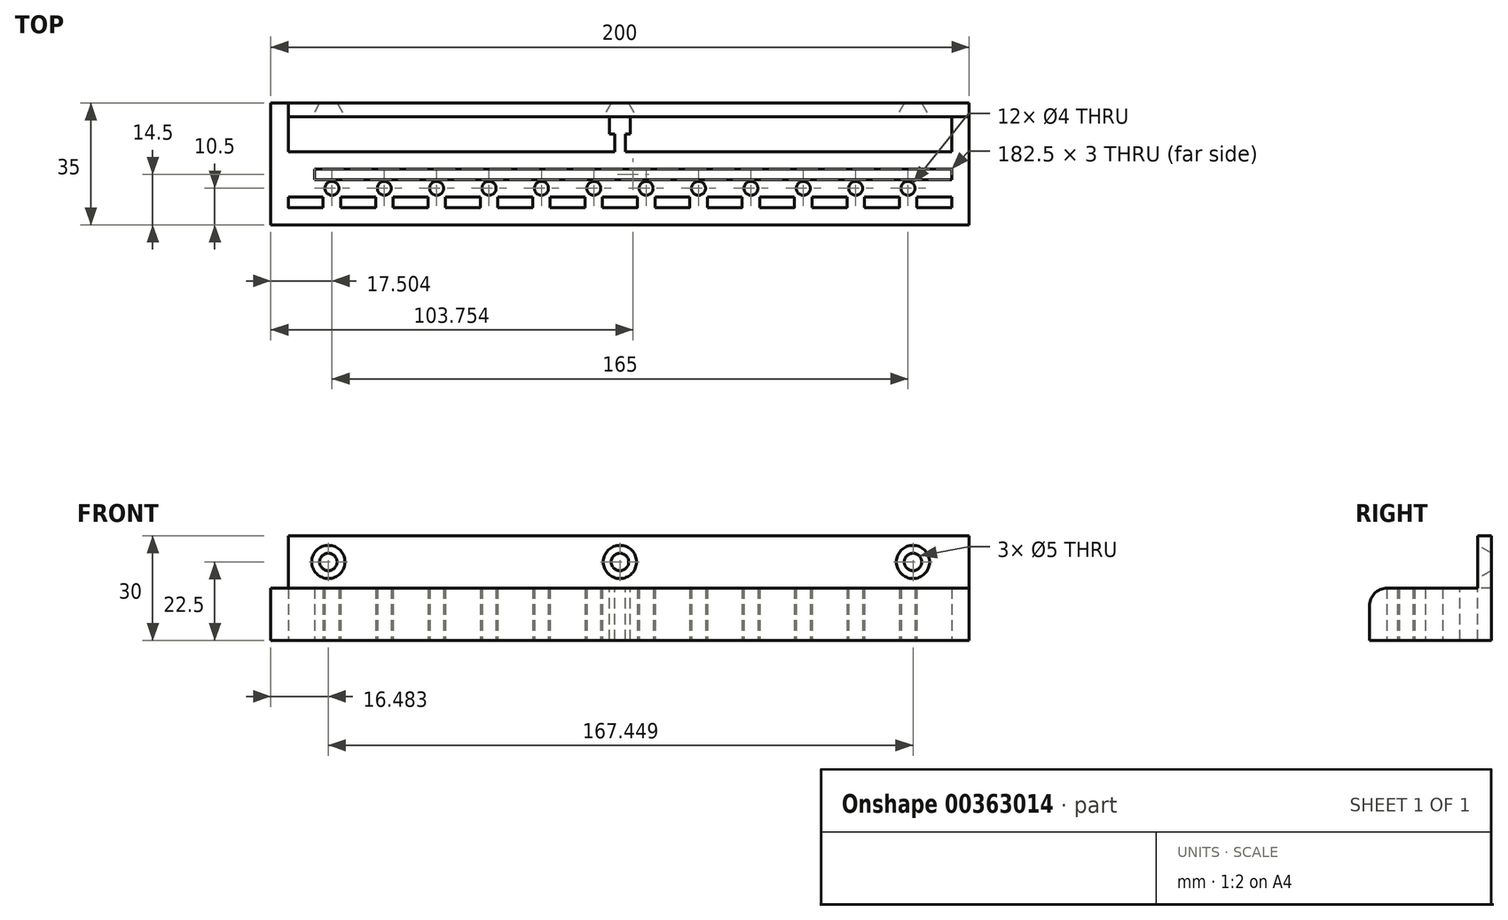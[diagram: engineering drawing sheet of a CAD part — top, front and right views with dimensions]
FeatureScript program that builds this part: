
annotation { "Feature Type Name" : "Feature", "Feature Type Description" : "" }
export const myFeature = defineFeature(function(context is Context, id is Id, definition is map)
    precondition{}
    {
        {
            var Q0;
            Q0=qCreatedBy(makeId("Top.planeOp"),FACE);
            var sketch = newSketch(context, id + "F0", { "sketchPlane" : qUnion([Q0])});
            skLineSegment(sketch, "E0.bottom", {"start": v(-101.4, -11.15) * mm, "end": v(98.6, -11.15) * mm});
            skLineSegment(sketch, "E0.top", {"start": v(-101.4, -32.15) * mm, "end": v(98.6, -32.15) * mm});
            skLineSegment(sketch, "E0.left", {"start": v(-101.4, -11.15) * mm, "end": v(-101.4, -32.15) * mm});
            skLineSegment(sketch, "E0.right", {"start": v(98.6, -11.15) * mm, "end": v(98.6, -32.15) * mm});
            skLineSegment(sketch, "E1", {"start": v(-101.4, -32.15) * mm, "end": v(-101.4, -27.15) * mm});
            skLineSegment(sketch, "E2", {"start": v(-101.4, -27.15) * mm, "end": v(98.6, -27.15) * mm});
            skLineSegment(sketch, "E3", {"start": v(98.6, -27.15) * mm, "end": v(98.6, -24.15) * mm});
            skLineSegment(sketch, "E4", {"start": v(98.6, -24.15) * mm, "end": v(-101.4, -24.15) * mm});
            skLineSegment(sketch, "E5", {"start": v(-101.4, -24.15) * mm, "end": v(-101.4, -19.15) * mm});
            skLineSegment(sketch, "E6", {"start": v(-101.4, -19.15) * mm, "end": v(98.6, -19.15) * mm});
            skLineSegment(sketch, "E7", {"start": v(98.6, -19.15) * mm, "end": v(98.6, -16.15) * mm});
            skLineSegment(sketch, "E8", {"start": v(98.6, -16.15) * mm, "end": v(-101.4, -16.15) * mm});
            skLineSegment(sketch, "E9", {"start": v(-101.4, -11.15) * mm, "end": v(-96.4, -11.15) * mm});
            skLineSegment(sketch, "E10", {"start": v(-96.4, -11.15) * mm, "end": v(-96.4, -32.15) * mm});
            skLineSegment(sketch, "E11", {"start": v(-96.4, -32.15) * mm, "end": v(-86.4, -32.15) * mm});
            skLineSegment(sketch, "E12", {"start": v(-86.4, -32.15) * mm, "end": v(-81.4, -32.15) * mm});
            skLineSegment(sketch, "E13", {"start": v(-81.4, -32.15) * mm, "end": v(-71.4, -32.15) * mm});
            skLineSegment(sketch, "E14", {"start": v(-71.4, -32.15) * mm, "end": v(-66.4, -32.15) * mm});
            skLineSegment(sketch, "E15", {"start": v(-66.4, -32.15) * mm, "end": v(-56.4, -32.15) * mm});
            skLineSegment(sketch, "E16", {"start": v(-56.4, -32.15) * mm, "end": v(-51.4, -32.15) * mm});
            skLineSegment(sketch, "E17", {"start": v(-51.4, -32.15) * mm, "end": v(-41.4, -32.15) * mm});
            skLineSegment(sketch, "E18", {"start": v(-41.4, -32.15) * mm, "end": v(-36.4, -32.15) * mm});
            skLineSegment(sketch, "E19", {"start": v(-36.4, -32.15) * mm, "end": v(-26.4, -32.15) * mm});
            skLineSegment(sketch, "E20", {"start": v(-26.4, -32.15) * mm, "end": v(-21.4, -32.15) * mm});
            skLineSegment(sketch, "E21", {"start": v(-21.4, -32.15) * mm, "end": v(-11.4, -32.15) * mm});
            skLineSegment(sketch, "E22", {"start": v(-11.4, -32.15) * mm, "end": v(-6.4, -32.15) * mm});
            skLineSegment(sketch, "E23", {"start": v(-6.4, -32.15) * mm, "end": v(3.6, -32.15) * mm});
            skLineSegment(sketch, "E24", {"start": v(3.6, -32.15) * mm, "end": v(8.6, -32.15) * mm});
            skLineSegment(sketch, "E25", {"start": v(8.6, -32.15) * mm, "end": v(18.6, -32.15) * mm});
            skLineSegment(sketch, "E26", {"start": v(18.6, -32.15) * mm, "end": v(23.6, -32.15) * mm});
            skLineSegment(sketch, "E27", {"start": v(23.6, -32.15) * mm, "end": v(33.6, -32.15) * mm});
            skLineSegment(sketch, "E28", {"start": v(33.6, -32.15) * mm, "end": v(38.6, -32.15) * mm});
            skLineSegment(sketch, "E29", {"start": v(38.6, -32.15) * mm, "end": v(48.6, -32.15) * mm});
            skLineSegment(sketch, "E30", {"start": v(48.6, -32.15) * mm, "end": v(53.6, -32.15) * mm});
            skLineSegment(sketch, "E31", {"start": v(53.6, -32.15) * mm, "end": v(63.6, -32.15) * mm});
            skLineSegment(sketch, "E32", {"start": v(63.6, -32.15) * mm, "end": v(68.6, -32.15) * mm});
            skLineSegment(sketch, "E33", {"start": v(68.6, -32.15) * mm, "end": v(78.6, -32.15) * mm});
            skLineSegment(sketch, "E34", {"start": v(78.6, -32.15) * mm, "end": v(83.6, -32.15) * mm});
            skLineSegment(sketch, "E35", {"start": v(83.6, -32.15) * mm, "end": v(93.6, -32.15) * mm});
            skLineSegment(sketch, "E36", {"start": v(93.6, -32.15) * mm, "end": v(98.6, -32.15) * mm});
            skLineSegment(sketch, "E37", {"start": v(93.6, -32.15) * mm, "end": v(93.6, -11.15) * mm});
            skLineSegment(sketch, "E38", {"start": v(-86.4, -32.15) * mm, "end": v(-86.4, -11.15) * mm});
            skLineSegment(sketch, "E39", {"start": v(-81.4, -32.15) * mm, "end": v(-81.4, -11.15) * mm});
            skLineSegment(sketch, "E40", {"start": v(-81.4, -11.15) * mm, "end": v(-71.4, -11.15) * mm});
            skLineSegment(sketch, "E41", {"start": v(-71.4, -11.15) * mm, "end": v(-71.4, -32.15) * mm});
            skLineSegment(sketch, "E42", {"start": v(-66.4, -32.15) * mm, "end": v(-66.4, -11.15) * mm});
            skLineSegment(sketch, "E43", {"start": v(-66.4, -11.15) * mm, "end": v(-56.4, -11.15) * mm});
            skLineSegment(sketch, "E44", {"start": v(-56.4, -11.15) * mm, "end": v(-56.4, -32.15) * mm});
            skLineSegment(sketch, "E45", {"start": v(-51.4, -32.15) * mm, "end": v(-51.4, -11.15) * mm});
            skLineSegment(sketch, "E46", {"start": v(-51.4, -11.15) * mm, "end": v(-41.4, -11.15) * mm});
            skLineSegment(sketch, "E47", {"start": v(-41.4, -11.15) * mm, "end": v(-41.4, -32.15) * mm});
            skLineSegment(sketch, "E48", {"start": v(-36.4, -32.15) * mm, "end": v(-36.4, -11.15) * mm});
            skLineSegment(sketch, "E49", {"start": v(-36.4, -11.15) * mm, "end": v(-26.4, -11.15) * mm});
            skLineSegment(sketch, "E50", {"start": v(-26.4, -11.15) * mm, "end": v(-26.4, -32.15) * mm});
            skLineSegment(sketch, "E51", {"start": v(-21.4, -32.15) * mm, "end": v(-21.4, -11.15) * mm});
            skLineSegment(sketch, "E52", {"start": v(-21.4, -11.15) * mm, "end": v(-11.4, -11.15) * mm});
            skLineSegment(sketch, "E53", {"start": v(-11.4, -11.15) * mm, "end": v(-11.4, -32.15) * mm});
            skLineSegment(sketch, "E54", {"start": v(-6.4, -32.15) * mm, "end": v(-6.4, -11.15) * mm});
            skLineSegment(sketch, "E55", {"start": v(-6.4, -11.15) * mm, "end": v(3.6, -11.15) * mm});
            skLineSegment(sketch, "E56", {"start": v(3.6, -11.15) * mm, "end": v(3.6, -32.15) * mm});
            skLineSegment(sketch, "E57", {"start": v(8.6, -32.15) * mm, "end": v(8.6, -11.15) * mm});
            skLineSegment(sketch, "E58", {"start": v(8.6, -11.15) * mm, "end": v(18.6, -11.15) * mm});
            skLineSegment(sketch, "E59", {"start": v(18.6, -11.15) * mm, "end": v(18.6, -32.15) * mm});
            skLineSegment(sketch, "E60", {"start": v(23.6, -32.15) * mm, "end": v(23.6, -11.15) * mm});
            skLineSegment(sketch, "E61", {"start": v(23.6, -11.15) * mm, "end": v(33.6, -11.15) * mm});
            skLineSegment(sketch, "E62", {"start": v(33.6, -11.15) * mm, "end": v(33.6, -32.15) * mm});
            skLineSegment(sketch, "E63", {"start": v(38.6, -32.15) * mm, "end": v(38.6, -11.15) * mm});
            skLineSegment(sketch, "E64", {"start": v(38.6, -11.15) * mm, "end": v(48.6, -11.15) * mm});
            skLineSegment(sketch, "E65", {"start": v(48.6, -11.15) * mm, "end": v(48.6, -32.15) * mm});
            skLineSegment(sketch, "E66", {"start": v(53.6, -32.15) * mm, "end": v(53.6, -11.15) * mm});
            skLineSegment(sketch, "E67", {"start": v(53.6, -11.15) * mm, "end": v(63.6, -11.15) * mm});
            skLineSegment(sketch, "E68", {"start": v(63.6, -11.15) * mm, "end": v(63.6, -32.15) * mm});
            skLineSegment(sketch, "E69", {"start": v(68.6, -32.15) * mm, "end": v(68.6, -11.15) * mm});
            skLineSegment(sketch, "E70", {"start": v(68.6, -11.15) * mm, "end": v(78.6, -11.15) * mm});
            skLineSegment(sketch, "E71", {"start": v(78.6, -11.15) * mm, "end": v(78.6, -32.15) * mm});
            skLineSegment(sketch, "E72", {"start": v(83.6, -32.15) * mm, "end": v(83.6, -11.15) * mm});
            skLineSegment(sketch, "E73", {"start": v(-86.4, -16.15) * mm, "end": v(-88.9, -16.15) * mm});
            skLineSegment(sketch, "E74", {"start": v(-88.9, -16.15) * mm, "end": v(-78.9, -16.15) * mm});
            skLineSegment(sketch, "E75", {"start": v(-78.9, -16.15) * mm, "end": v(-73.9, -16.15) * mm});
            skLineSegment(sketch, "E76", {"start": v(-73.9, -16.15) * mm, "end": v(-63.9, -16.15) * mm});
            skLineSegment(sketch, "E77", {"start": v(-63.9, -16.15) * mm, "end": v(-58.9, -16.15) * mm});
            skLineSegment(sketch, "E78", {"start": v(-58.9, -16.15) * mm, "end": v(-48.9, -16.15) * mm});
            skLineSegment(sketch, "E79", {"start": v(-48.9, -16.15) * mm, "end": v(-43.9, -16.15) * mm});
            skLineSegment(sketch, "E80", {"start": v(-43.9, -16.15) * mm, "end": v(-33.9, -16.15) * mm});
            skLineSegment(sketch, "E81", {"start": v(-33.9, -16.15) * mm, "end": v(-28.9, -16.15) * mm});
            skLineSegment(sketch, "E82", {"start": v(-28.9, -16.15) * mm, "end": v(-18.9, -16.15) * mm});
            skLineSegment(sketch, "E83", {"start": v(-18.9, -16.15) * mm, "end": v(-13.9, -16.15) * mm});
            skLineSegment(sketch, "E84", {"start": v(-13.9, -16.15) * mm, "end": v(-3.9, -16.15) * mm});
            skLineSegment(sketch, "E85", {"start": v(-3.9, -16.15) * mm, "end": v(1.1, -16.15) * mm});
            skLineSegment(sketch, "E86", {"start": v(1.1, -16.15) * mm, "end": v(11.1, -16.15) * mm});
            skLineSegment(sketch, "E87", {"start": v(11.1, -16.15) * mm, "end": v(16.1, -16.15) * mm});
            skLineSegment(sketch, "E88", {"start": v(16.1, -16.15) * mm, "end": v(26.1, -16.15) * mm});
            skLineSegment(sketch, "E89", {"start": v(26.1, -16.15) * mm, "end": v(31.1, -16.15) * mm});
            skLineSegment(sketch, "E90", {"start": v(31.1, -16.15) * mm, "end": v(41.1, -16.15) * mm});
            skLineSegment(sketch, "E91", {"start": v(41.1, -16.15) * mm, "end": v(46.1, -16.15) * mm});
            skLineSegment(sketch, "E92", {"start": v(46.1, -16.15) * mm, "end": v(56.1, -16.15) * mm});
            skLineSegment(sketch, "E93", {"start": v(56.1, -16.15) * mm, "end": v(61.1, -16.15) * mm});
            skLineSegment(sketch, "E94", {"start": v(61.1, -16.15) * mm, "end": v(71.1, -16.15) * mm});
            skLineSegment(sketch, "E95", {"start": v(71.1, -16.15) * mm, "end": v(76.1, -16.15) * mm});
            skLineSegment(sketch, "E96", {"start": v(76.1, -16.15) * mm, "end": v(86.1, -16.15) * mm});
            skLineSegment(sketch, "E97", {"start": v(86.1, -16.15) * mm, "end": v(91.1, -16.15) * mm});
            skLineSegment(sketch, "E98", {"start": v(86.1, -16.15) * mm, "end": v(86.1, -19.15) * mm});
            skLineSegment(sketch, "E99", {"start": v(86.1, -19.15) * mm, "end": v(76.1, -19.15) * mm});
            skLineSegment(sketch, "E100", {"start": v(76.1, -19.15) * mm, "end": v(76.1, -16.15) * mm});
            skLineSegment(sketch, "E101", {"start": v(71.1, -16.15) * mm, "end": v(71.1, -19.15) * mm});
            skLineSegment(sketch, "E102", {"start": v(71.1, -19.15) * mm, "end": v(61.1, -19.15) * mm});
            skLineSegment(sketch, "E103", {"start": v(61.1, -19.15) * mm, "end": v(61.1, -16.15) * mm});
            skLineSegment(sketch, "E104", {"start": v(56.1, -16.15) * mm, "end": v(56.1, -19.15) * mm});
            skLineSegment(sketch, "E105", {"start": v(56.1, -19.15) * mm, "end": v(46.1, -19.15) * mm});
            skLineSegment(sketch, "E106", {"start": v(46.1, -19.15) * mm, "end": v(46.1, -16.15) * mm});
            skLineSegment(sketch, "E107", {"start": v(41.1, -16.15) * mm, "end": v(41.1, -19.15) * mm});
            skLineSegment(sketch, "E108", {"start": v(41.1, -19.15) * mm, "end": v(31.1, -19.15) * mm});
            skLineSegment(sketch, "E109", {"start": v(31.1, -19.15) * mm, "end": v(31.1, -16.15) * mm});
            skLineSegment(sketch, "E110", {"start": v(26.1, -16.15) * mm, "end": v(26.1, -19.15) * mm});
            skLineSegment(sketch, "E111", {"start": v(26.1, -19.15) * mm, "end": v(16.1, -19.15) * mm});
            skLineSegment(sketch, "E112", {"start": v(16.1, -19.15) * mm, "end": v(16.1, -16.15) * mm});
            skLineSegment(sketch, "E113", {"start": v(11.1, -16.15) * mm, "end": v(11.1, -19.15) * mm});
            skLineSegment(sketch, "E114", {"start": v(11.1, -19.15) * mm, "end": v(1.1, -19.15) * mm});
            skLineSegment(sketch, "E115", {"start": v(1.1, -19.15) * mm, "end": v(1.1, -16.15) * mm});
            skLineSegment(sketch, "E116", {"start": v(-3.9, -16.15) * mm, "end": v(-3.9, -19.15) * mm});
            skLineSegment(sketch, "E117", {"start": v(-3.9, -19.15) * mm, "end": v(-13.9, -19.15) * mm});
            skLineSegment(sketch, "E118", {"start": v(-13.9, -19.15) * mm, "end": v(-13.9, -16.15) * mm});
            skLineSegment(sketch, "E119", {"start": v(-18.9, -16.15) * mm, "end": v(-18.9, -19.15) * mm});
            skLineSegment(sketch, "E120", {"start": v(-18.9, -19.15) * mm, "end": v(-28.9, -19.15) * mm});
            skLineSegment(sketch, "E121", {"start": v(-28.9, -19.15) * mm, "end": v(-28.9, -16.15) * mm});
            skLineSegment(sketch, "E122", {"start": v(-33.9, -16.15) * mm, "end": v(-33.9, -19.15) * mm});
            skLineSegment(sketch, "E123", {"start": v(-33.9, -19.15) * mm, "end": v(-43.9, -19.15) * mm});
            skLineSegment(sketch, "E124", {"start": v(-43.9, -19.15) * mm, "end": v(-43.9, -16.15) * mm});
            skLineSegment(sketch, "E125", {"start": v(-48.9, -16.15) * mm, "end": v(-48.9, -19.15) * mm});
            skLineSegment(sketch, "E126", {"start": v(-48.9, -19.15) * mm, "end": v(-58.9, -19.15) * mm});
            skLineSegment(sketch, "E127", {"start": v(-58.9, -19.15) * mm, "end": v(-58.9, -16.15) * mm});
            skLineSegment(sketch, "E128", {"start": v(-63.9, -16.15) * mm, "end": v(-63.9, -19.15) * mm});
            skLineSegment(sketch, "E129", {"start": v(-63.9, -19.15) * mm, "end": v(-73.9, -19.15) * mm});
            skLineSegment(sketch, "E130", {"start": v(-73.9, -19.15) * mm, "end": v(-73.9, -16.15) * mm});
            skLineSegment(sketch, "E131", {"start": v(-78.9, -16.15) * mm, "end": v(-78.9, -19.15) * mm});
            skLineSegment(sketch, "E132", {"start": v(-78.9, -19.15) * mm, "end": v(-88.9, -19.15) * mm});
            skLineSegment(sketch, "E133", {"start": v(-88.9, -19.15) * mm, "end": v(-88.9, -16.15) * mm});
            skLineSegment(sketch, "E134", {"start": v(-81.4, -24.15) * mm, "end": v(-81.4, -21.65) * mm});
            skLineSegment(sketch, "E135", {"start": v(-81.4, -21.65) * mm, "end": v(-83.9, -21.65) * mm});
            skPoint(sketch, "E135.endSnap0", {"position": v(-83.9, -19.15) * mm});
            skCircle(sketch, "E136", {"center": v(-83.9, -21.65) * mm, "radius": 2 * mm});
            skLineSegment(sketch, "E137", {"start": v(-71.4, -24.15) * mm, "end": v(-71.4, -21.65) * mm});
            skLineSegment(sketch, "E138", {"start": v(-71.4, -21.65) * mm, "end": v(-68.9, -21.65) * mm});
            skPoint(sketch, "E138.endSnap0", {"position": v(-68.9, -19.15) * mm});
            skLineSegment(sketch, "E139", {"start": v(-56.4, -24.15) * mm, "end": v(-53.9, -21.65) * mm});
            skPoint(sketch, "E139.endSnap0", {"position": v(-53.9, -19.15) * mm});
            skPoint(sketch, "E139.endSnap1", {"position": v(-56.4, -21.65) * mm});
            skLineSegment(sketch, "E140", {"start": v(-41.4, -24.15) * mm, "end": v(-38.9, -21.65) * mm});
            skPoint(sketch, "E140.endSnap0", {"position": v(-36.4, -21.65) * mm});
            skPoint(sketch, "E140.endSnap1", {"position": v(-38.9, -19.15) * mm});
            skLineSegment(sketch, "E141", {"start": v(-26.4, -24.15) * mm, "end": v(-26.4, -21.65) * mm});
            skLineSegment(sketch, "E142", {"start": v(-26.4, -21.65) * mm, "end": v(-23.9, -21.65) * mm});
            skPoint(sketch, "E142.endSnap0", {"position": v(-23.9, -19.15) * mm});
            skLineSegment(sketch, "E143", {"start": v(-11.4, -24.15) * mm, "end": v(-11.4, -21.65) * mm});
            skLineSegment(sketch, "E144", {"start": v(-11.4, -21.65) * mm, "end": v(-8.9, -21.65) * mm});
            skPoint(sketch, "E144.endSnap0", {"position": v(-8.9, -19.15) * mm});
            skLineSegment(sketch, "E145", {"start": v(3.6, -24.15) * mm, "end": v(6.1, -21.65) * mm});
            skPoint(sketch, "E145.endSnap0", {"position": v(6.1, -19.15) * mm});
            skPoint(sketch, "E145.endSnap1", {"position": v(8.6, -21.65) * mm});
            skLineSegment(sketch, "E146", {"start": v(18.6, -24.15) * mm, "end": v(18.6, -19.15) * mm});
            skPoint(sketch, "E146.endSnap0", {"position": v(21.1, -19.15) * mm});
            skLineSegment(sketch, "E147", {"start": v(18.6, -19.15) * mm, "end": v(21.1, -19.15) * mm});
            skLineSegment(sketch, "E148", {"start": v(18.6, -24.15) * mm, "end": v(18.6, -21.65) * mm});
            skLineSegment(sketch, "E149", {"start": v(18.6, -21.65) * mm, "end": v(21.1, -21.65) * mm});
            skLineSegment(sketch, "E150", {"start": v(33.6, -24.15) * mm, "end": v(33.6, -21.65) * mm});
            skPoint(sketch, "E150.startSnap0", {"position": v(33.6, -21.65) * mm});
            skLineSegment(sketch, "E151", {"start": v(33.6, -21.65) * mm, "end": v(36.1, -21.65) * mm});
            skPoint(sketch, "E151.endSnap0", {"position": v(36.1, -19.15) * mm});
            skLineSegment(sketch, "E152", {"start": v(48.6, -24.15) * mm, "end": v(48.6, -21.65) * mm});
            skLineSegment(sketch, "E153", {"start": v(48.6, -21.65) * mm, "end": v(51.1, -21.65) * mm});
            skPoint(sketch, "E153.endSnap0", {"position": v(51.1, -19.15) * mm});
            skLineSegment(sketch, "E154", {"start": v(63.6, -24.15) * mm, "end": v(63.6, -21.65) * mm});
            skLineSegment(sketch, "E155", {"start": v(63.6, -21.65) * mm, "end": v(66.1, -21.65) * mm});
            skPoint(sketch, "E155.endSnap0", {"position": v(66.1, -19.15) * mm});
            skLineSegment(sketch, "E156", {"start": v(78.6, -24.15) * mm, "end": v(78.6, -21.65) * mm});
            skLineSegment(sketch, "E157", {"start": v(78.6, -21.65) * mm, "end": v(81.1, -21.65) * mm});
            skPoint(sketch, "E157.endSnap0", {"position": v(81.1, -19.15) * mm});
            skCircle(sketch, "E158", {"center": v(81.1, -21.65) * mm, "radius": 2 * mm});
            skCircle(sketch, "E159", {"center": v(66.1, -21.65) * mm, "radius": 2 * mm});
            skCircle(sketch, "E160", {"center": v(51.1, -21.65) * mm, "radius": 2 * mm});
            skCircle(sketch, "E161", {"center": v(36.1, -21.65) * mm, "radius": 2 * mm});
            skCircle(sketch, "E162", {"center": v(21.1, -21.65) * mm, "radius": 2 * mm});
            skCircle(sketch, "E163", {"center": v(6.1, -21.65) * mm, "radius": 2 * mm});
            skCircle(sketch, "E164", {"center": v(-8.9, -21.65) * mm, "radius": 2 * mm});
            skCircle(sketch, "E165", {"center": v(-23.9, -21.65) * mm, "radius": 2 * mm});
            skCircle(sketch, "E166", {"center": v(-38.9, -21.65) * mm, "radius": 2 * mm});
            skCircle(sketch, "E167", {"center": v(-53.9, -21.65) * mm, "radius": 2 * mm});
            skCircle(sketch, "E168", {"center": v(-68.9, -21.65) * mm, "radius": 2 * mm});
            skSolve(sketch);
        }
        {
            var Q0;
            Q0 = qSketchRegion(id + "F0", true);
            var Q1;
            {var subQ0=sQuery(id+"F0.wireOp",EDGE,"E133");Q1=makeQuery(id+"F0.imprint","IMPRINT",FACE,{"disambiguationData":[TD([[makeQuery(id+"F0.imprint","IMPRINT",EDGE,{"derivedFrom":subQ0}),1.0]])]});}
            var Q2;
            {var subQ0=sQuery(id+"F0.wireOp",EDGE,"E38");var subQ1=sQuery(id+"F0.wireOp",EDGE,"E4");var subQ2=makeQuery(id+"F0.imprint","INTERSECT",VERTEX,{"derivedFrom":[subQ1,subQ0]});Q2=makeQuery(id+"F0.imprint","IMPRINT",FACE,{"disambiguationData":[TD([[makeQuery(id+"F0.imprint","IMPRINT",EDGE,{"disambiguationData":[TD([[subQ2,-1.0]])],"derivedFrom":subQ1}),-1.0]])]});}
            var Q3;
            {var subQ0=sQuery(id+"F0.wireOp",EDGE,"E39");var subQ1=sQuery(id+"F0.wireOp",EDGE,"E4");var subQ2=makeQuery(id+"F0.imprint","INTERSECT",VERTEX,{"derivedFrom":[subQ1,subQ0]});Q3=makeQuery(id+"F0.imprint","IMPRINT",FACE,{"disambiguationData":[TD([[makeQuery(id+"F0.imprint","IMPRINT",EDGE,{"disambiguationData":[TD([[subQ2,-1.0]])],"derivedFrom":subQ1}),-1.0]])]});}
            var Q4;
            {var subQ1=sQuery(id+"F0.wireOp",EDGE,"E4");var subQ9=sQuery(id+"F0.wireOp",EDGE,"E41");var subQ10=makeQuery(id+"F0.imprint","INTERSECT",VERTEX,{"derivedFrom":[subQ1,subQ9]});Q4=makeQuery(id+"F0.imprint","IMPRINT",FACE,{"disambiguationData":[TD([[makeQuery(id+"F0.imprint","IMPRINT",EDGE,{"disambiguationData":[TD([[subQ10,-1.0]])],"derivedFrom":subQ1}),-1.0]])]});}
            var Q5;
            {var subQ0=sQuery(id+"F0.wireOp",EDGE,"E42");var subQ1=sQuery(id+"F0.wireOp",EDGE,"E4");var subQ2=makeQuery(id+"F0.imprint","INTERSECT",VERTEX,{"derivedFrom":[subQ1,subQ0]});Q5=makeQuery(id+"F0.imprint","IMPRINT",FACE,{"disambiguationData":[TD([[makeQuery(id+"F0.imprint","IMPRINT",EDGE,{"disambiguationData":[TD([[subQ2,-1.0]])],"derivedFrom":subQ1}),-1.0]])]});}
            var Q6;
            {var subQ0=sQuery(id+"F0.wireOp",EDGE,"E44");var subQ1=sQuery(id+"F0.wireOp",EDGE,"E4");var subQ2=makeQuery(id+"F0.imprint","INTERSECT",VERTEX,{"derivedFrom":[subQ1,subQ0]});Q6=makeQuery(id+"F0.imprint","IMPRINT",FACE,{"disambiguationData":[TD([[makeQuery(id+"F0.imprint","IMPRINT",EDGE,{"disambiguationData":[TD([[subQ2,-1.0]])],"derivedFrom":subQ1}),-1.0]])]});}
            var Q7;
            {var subQ0=sQuery(id+"F0.wireOp",EDGE,"E45");var subQ1=sQuery(id+"F0.wireOp",EDGE,"E4");var subQ2=makeQuery(id+"F0.imprint","INTERSECT",VERTEX,{"derivedFrom":[subQ1,subQ0]});Q7=makeQuery(id+"F0.imprint","IMPRINT",FACE,{"disambiguationData":[TD([[makeQuery(id+"F0.imprint","IMPRINT",EDGE,{"disambiguationData":[TD([[subQ2,-1.0]])],"derivedFrom":subQ1}),-1.0]])]});}
            var Q8;
            {var subQ0=sQuery(id+"F0.wireOp",EDGE,"E47");var subQ1=sQuery(id+"F0.wireOp",EDGE,"E4");var subQ2=makeQuery(id+"F0.imprint","INTERSECT",VERTEX,{"derivedFrom":[subQ1,subQ0]});Q8=makeQuery(id+"F0.imprint","IMPRINT",FACE,{"disambiguationData":[TD([[makeQuery(id+"F0.imprint","IMPRINT",EDGE,{"disambiguationData":[TD([[subQ2,-1.0]])],"derivedFrom":subQ1}),-1.0]])]});}
            var Q9;
            {var subQ0=sQuery(id+"F0.wireOp",EDGE,"E48");var subQ1=sQuery(id+"F0.wireOp",EDGE,"E4");var subQ2=makeQuery(id+"F0.imprint","INTERSECT",VERTEX,{"derivedFrom":[subQ1,subQ0]});Q9=makeQuery(id+"F0.imprint","IMPRINT",FACE,{"disambiguationData":[TD([[makeQuery(id+"F0.imprint","IMPRINT",EDGE,{"disambiguationData":[TD([[subQ2,-1.0]])],"derivedFrom":subQ1}),-1.0]])]});}
            var Q10;
            {var subQ0=sQuery(id+"F0.wireOp",EDGE,"E50");var subQ1=sQuery(id+"F0.wireOp",EDGE,"E4");var subQ2=makeQuery(id+"F0.imprint","INTERSECT",VERTEX,{"derivedFrom":[subQ1,subQ0]});Q10=makeQuery(id+"F0.imprint","IMPRINT",FACE,{"disambiguationData":[TD([[makeQuery(id+"F0.imprint","IMPRINT",EDGE,{"disambiguationData":[TD([[subQ2,-1.0]])],"derivedFrom":subQ1}),-1.0]])]});}
            var Q11;
            {var subQ0=sQuery(id+"F0.wireOp",EDGE,"E51");var subQ1=sQuery(id+"F0.wireOp",EDGE,"E4");var subQ2=makeQuery(id+"F0.imprint","INTERSECT",VERTEX,{"derivedFrom":[subQ1,subQ0]});Q11=makeQuery(id+"F0.imprint","IMPRINT",FACE,{"disambiguationData":[TD([[makeQuery(id+"F0.imprint","IMPRINT",EDGE,{"disambiguationData":[TD([[subQ2,-1.0]])],"derivedFrom":subQ1}),-1.0]])]});}
            var Q12;
            {var subQ0=sQuery(id+"F0.wireOp",EDGE,"E53");var subQ1=sQuery(id+"F0.wireOp",EDGE,"E4");var subQ2=makeQuery(id+"F0.imprint","INTERSECT",VERTEX,{"derivedFrom":[subQ1,subQ0]});Q12=makeQuery(id+"F0.imprint","IMPRINT",FACE,{"disambiguationData":[TD([[makeQuery(id+"F0.imprint","IMPRINT",EDGE,{"disambiguationData":[TD([[subQ2,-1.0]])],"derivedFrom":subQ1}),-1.0]])]});}
            var Q13;
            {var subQ0=sQuery(id+"F0.wireOp",EDGE,"E54");var subQ1=sQuery(id+"F0.wireOp",EDGE,"E4");var subQ2=makeQuery(id+"F0.imprint","INTERSECT",VERTEX,{"derivedFrom":[subQ1,subQ0]});Q13=makeQuery(id+"F0.imprint","IMPRINT",FACE,{"disambiguationData":[TD([[makeQuery(id+"F0.imprint","IMPRINT",EDGE,{"disambiguationData":[TD([[subQ2,-1.0]])],"derivedFrom":subQ1}),-1.0]])]});}
            var Q14;
            {var subQ1=sQuery(id+"F0.wireOp",EDGE,"E4");var subQ9=sQuery(id+"F0.wireOp",EDGE,"E56");var subQ10=makeQuery(id+"F0.imprint","INTERSECT",VERTEX,{"derivedFrom":[subQ1,subQ9]});Q14=makeQuery(id+"F0.imprint","IMPRINT",FACE,{"disambiguationData":[TD([[makeQuery(id+"F0.imprint","IMPRINT",EDGE,{"disambiguationData":[TD([[subQ10,-1.0]])],"derivedFrom":subQ1}),-1.0]])]});}
            var Q15;
            {var subQ0=sQuery(id+"F0.wireOp",EDGE,"E57");var subQ1=sQuery(id+"F0.wireOp",EDGE,"E4");var subQ2=makeQuery(id+"F0.imprint","INTERSECT",VERTEX,{"derivedFrom":[subQ1,subQ0]});Q15=makeQuery(id+"F0.imprint","IMPRINT",FACE,{"disambiguationData":[TD([[makeQuery(id+"F0.imprint","IMPRINT",EDGE,{"disambiguationData":[TD([[subQ2,-1.0]])],"derivedFrom":subQ1}),-1.0]])]});}
            var Q16;
            {var subQ0=sQuery(id+"F0.wireOp",EDGE,"E59");var subQ1=sQuery(id+"F0.wireOp",EDGE,"E4");var subQ2=makeQuery(id+"F0.imprint","INTERSECT",VERTEX,{"derivedFrom":[subQ1,subQ0]});Q16=makeQuery(id+"F0.imprint","IMPRINT",FACE,{"disambiguationData":[TD([[makeQuery(id+"F0.imprint","IMPRINT",EDGE,{"disambiguationData":[TD([[subQ2,-1.0]])],"derivedFrom":subQ1}),-1.0]])]});}
            var Q17;
            {var subQ0=sQuery(id+"F0.wireOp",EDGE,"E60");var subQ1=sQuery(id+"F0.wireOp",EDGE,"E4");var subQ2=makeQuery(id+"F0.imprint","INTERSECT",VERTEX,{"derivedFrom":[subQ1,subQ0]});Q17=makeQuery(id+"F0.imprint","IMPRINT",FACE,{"disambiguationData":[TD([[makeQuery(id+"F0.imprint","IMPRINT",EDGE,{"disambiguationData":[TD([[subQ2,-1.0]])],"derivedFrom":subQ1}),-1.0]])]});}
            var Q18;
            {var subQ0=sQuery(id+"F0.wireOp",EDGE,"E62");var subQ1=sQuery(id+"F0.wireOp",EDGE,"E4");var subQ2=makeQuery(id+"F0.imprint","INTERSECT",VERTEX,{"derivedFrom":[subQ1,subQ0]});Q18=makeQuery(id+"F0.imprint","IMPRINT",FACE,{"disambiguationData":[TD([[makeQuery(id+"F0.imprint","IMPRINT",EDGE,{"disambiguationData":[TD([[subQ2,-1.0]])],"derivedFrom":subQ1}),-1.0]])]});}
            var Q19;
            {var subQ0=sQuery(id+"F0.wireOp",EDGE,"E63");var subQ1=sQuery(id+"F0.wireOp",EDGE,"E4");var subQ2=makeQuery(id+"F0.imprint","INTERSECT",VERTEX,{"derivedFrom":[subQ1,subQ0]});Q19=makeQuery(id+"F0.imprint","IMPRINT",FACE,{"disambiguationData":[TD([[makeQuery(id+"F0.imprint","IMPRINT",EDGE,{"disambiguationData":[TD([[subQ2,-1.0]])],"derivedFrom":subQ1}),-1.0]])]});}
            var Q20;
            {var subQ0=sQuery(id+"F0.wireOp",EDGE,"E65");var subQ1=sQuery(id+"F0.wireOp",EDGE,"E4");var subQ2=makeQuery(id+"F0.imprint","INTERSECT",VERTEX,{"derivedFrom":[subQ1,subQ0]});Q20=makeQuery(id+"F0.imprint","IMPRINT",FACE,{"disambiguationData":[TD([[makeQuery(id+"F0.imprint","IMPRINT",EDGE,{"disambiguationData":[TD([[subQ2,-1.0]])],"derivedFrom":subQ1}),-1.0]])]});}
            var Q21;
            {var subQ0=sQuery(id+"F0.wireOp",EDGE,"E66");var subQ1=sQuery(id+"F0.wireOp",EDGE,"E4");var subQ2=makeQuery(id+"F0.imprint","INTERSECT",VERTEX,{"derivedFrom":[subQ1,subQ0]});Q21=makeQuery(id+"F0.imprint","IMPRINT",FACE,{"disambiguationData":[TD([[makeQuery(id+"F0.imprint","IMPRINT",EDGE,{"disambiguationData":[TD([[subQ2,-1.0]])],"derivedFrom":subQ1}),-1.0]])]});}
            var Q22;
            {var subQ0=sQuery(id+"F0.wireOp",EDGE,"E68");var subQ1=sQuery(id+"F0.wireOp",EDGE,"E4");var subQ2=makeQuery(id+"F0.imprint","INTERSECT",VERTEX,{"derivedFrom":[subQ1,subQ0]});Q22=makeQuery(id+"F0.imprint","IMPRINT",FACE,{"disambiguationData":[TD([[makeQuery(id+"F0.imprint","IMPRINT",EDGE,{"disambiguationData":[TD([[subQ2,-1.0]])],"derivedFrom":subQ1}),-1.0]])]});}
            var Q23;
            {var subQ0=sQuery(id+"F0.wireOp",EDGE,"E69");var subQ1=sQuery(id+"F0.wireOp",EDGE,"E4");var subQ2=makeQuery(id+"F0.imprint","INTERSECT",VERTEX,{"derivedFrom":[subQ1,subQ0]});Q23=makeQuery(id+"F0.imprint","IMPRINT",FACE,{"disambiguationData":[TD([[makeQuery(id+"F0.imprint","IMPRINT",EDGE,{"disambiguationData":[TD([[subQ2,-1.0]])],"derivedFrom":subQ1}),-1.0]])]});}
            var Q24;
            {var subQ1=sQuery(id+"F0.wireOp",EDGE,"E4");var subQ9=sQuery(id+"F0.wireOp",EDGE,"E71");var subQ10=makeQuery(id+"F0.imprint","INTERSECT",VERTEX,{"derivedFrom":[subQ1,subQ9]});Q24=makeQuery(id+"F0.imprint","IMPRINT",FACE,{"disambiguationData":[TD([[makeQuery(id+"F0.imprint","IMPRINT",EDGE,{"disambiguationData":[TD([[subQ10,-1.0]])],"derivedFrom":subQ1}),-1.0]])]});}
            var Q25;
            {var subQ0=sQuery(id+"F0.wireOp",EDGE,"E72");var subQ1=sQuery(id+"F0.wireOp",EDGE,"E4");var subQ2=makeQuery(id+"F0.imprint","INTERSECT",VERTEX,{"derivedFrom":[subQ1,subQ0]});Q25=makeQuery(id+"F0.imprint","IMPRINT",FACE,{"disambiguationData":[TD([[makeQuery(id+"F0.imprint","IMPRINT",EDGE,{"disambiguationData":[TD([[subQ2,-1.0]])],"derivedFrom":subQ1}),-1.0]])]});}
            var Q26;
            {var subQ1=sQuery(id+"F0.wireOp",EDGE,"E4");var subQ5=sQuery(id+"F0.wireOp",EDGE,"E37");var subQ6=makeQuery(id+"F0.imprint","INTERSECT",VERTEX,{"derivedFrom":[subQ1,subQ5]});Q26=makeQuery(id+"F0.imprint","IMPRINT",FACE,{"disambiguationData":[TD([[makeQuery(id+"F0.imprint","IMPRINT",EDGE,{"disambiguationData":[TD([[subQ6,-1.0]])],"derivedFrom":subQ1}),-1.0]])]});}
            var Q27;
            {var subQ0=sQuery(id+"F0.wireOp",EDGE,"E71");var subQ1=sQuery(id+"F0.wireOp",EDGE,"E2");var subQ2=makeQuery(id+"F0.imprint","INTERSECT",VERTEX,{"derivedFrom":[subQ1,subQ0]});Q27=makeQuery(id+"F0.imprint","IMPRINT",FACE,{"disambiguationData":[TD([[makeQuery(id+"F0.imprint","IMPRINT",EDGE,{"disambiguationData":[TD([[subQ2,-1.0]])],"derivedFrom":subQ1}),1.0]])]});}
            var Q28;
            {var subQ0=sQuery(id+"F0.wireOp",EDGE,"E68");var subQ1=sQuery(id+"F0.wireOp",EDGE,"E2");var subQ2=makeQuery(id+"F0.imprint","INTERSECT",VERTEX,{"derivedFrom":[subQ1,subQ0]});Q28=makeQuery(id+"F0.imprint","IMPRINT",FACE,{"disambiguationData":[TD([[makeQuery(id+"F0.imprint","IMPRINT",EDGE,{"disambiguationData":[TD([[subQ2,-1.0]])],"derivedFrom":subQ1}),1.0]])]});}
            var Q29;
            {var subQ0=sQuery(id+"F0.wireOp",EDGE,"E65");var subQ1=sQuery(id+"F0.wireOp",EDGE,"E2");var subQ2=makeQuery(id+"F0.imprint","INTERSECT",VERTEX,{"derivedFrom":[subQ1,subQ0]});Q29=makeQuery(id+"F0.imprint","IMPRINT",FACE,{"disambiguationData":[TD([[makeQuery(id+"F0.imprint","IMPRINT",EDGE,{"disambiguationData":[TD([[subQ2,-1.0]])],"derivedFrom":subQ1}),1.0]])]});}
            var Q30;
            {var subQ0=sQuery(id+"F0.wireOp",EDGE,"E62");var subQ1=sQuery(id+"F0.wireOp",EDGE,"E2");var subQ2=makeQuery(id+"F0.imprint","INTERSECT",VERTEX,{"derivedFrom":[subQ1,subQ0]});Q30=makeQuery(id+"F0.imprint","IMPRINT",FACE,{"disambiguationData":[TD([[makeQuery(id+"F0.imprint","IMPRINT",EDGE,{"disambiguationData":[TD([[subQ2,-1.0]])],"derivedFrom":subQ1}),1.0]])]});}
            var Q31;
            {var subQ0=sQuery(id+"F0.wireOp",EDGE,"E59");var subQ1=sQuery(id+"F0.wireOp",EDGE,"E2");var subQ2=makeQuery(id+"F0.imprint","INTERSECT",VERTEX,{"derivedFrom":[subQ1,subQ0]});Q31=makeQuery(id+"F0.imprint","IMPRINT",FACE,{"disambiguationData":[TD([[makeQuery(id+"F0.imprint","IMPRINT",EDGE,{"disambiguationData":[TD([[subQ2,-1.0]])],"derivedFrom":subQ1}),1.0]])]});}
            var Q32;
            {var subQ0=sQuery(id+"F0.wireOp",EDGE,"E56");var subQ1=sQuery(id+"F0.wireOp",EDGE,"E2");var subQ2=makeQuery(id+"F0.imprint","INTERSECT",VERTEX,{"derivedFrom":[subQ1,subQ0]});Q32=makeQuery(id+"F0.imprint","IMPRINT",FACE,{"disambiguationData":[TD([[makeQuery(id+"F0.imprint","IMPRINT",EDGE,{"disambiguationData":[TD([[subQ2,-1.0]])],"derivedFrom":subQ1}),1.0]])]});}
            var Q33;
            {var subQ0=sQuery(id+"F0.wireOp",EDGE,"E53");var subQ1=sQuery(id+"F0.wireOp",EDGE,"E2");var subQ2=makeQuery(id+"F0.imprint","INTERSECT",VERTEX,{"derivedFrom":[subQ1,subQ0]});Q33=makeQuery(id+"F0.imprint","IMPRINT",FACE,{"disambiguationData":[TD([[makeQuery(id+"F0.imprint","IMPRINT",EDGE,{"disambiguationData":[TD([[subQ2,-1.0]])],"derivedFrom":subQ1}),1.0]])]});}
            var Q34;
            {var subQ0=sQuery(id+"F0.wireOp",EDGE,"E50");var subQ1=sQuery(id+"F0.wireOp",EDGE,"E2");var subQ2=makeQuery(id+"F0.imprint","INTERSECT",VERTEX,{"derivedFrom":[subQ1,subQ0]});Q34=makeQuery(id+"F0.imprint","IMPRINT",FACE,{"disambiguationData":[TD([[makeQuery(id+"F0.imprint","IMPRINT",EDGE,{"disambiguationData":[TD([[subQ2,-1.0]])],"derivedFrom":subQ1}),1.0]])]});}
            var Q35;
            {var subQ0=sQuery(id+"F0.wireOp",EDGE,"E47");var subQ1=sQuery(id+"F0.wireOp",EDGE,"E2");var subQ2=makeQuery(id+"F0.imprint","INTERSECT",VERTEX,{"derivedFrom":[subQ1,subQ0]});Q35=makeQuery(id+"F0.imprint","IMPRINT",FACE,{"disambiguationData":[TD([[makeQuery(id+"F0.imprint","IMPRINT",EDGE,{"disambiguationData":[TD([[subQ2,-1.0]])],"derivedFrom":subQ1}),1.0]])]});}
            var Q36;
            {var subQ0=sQuery(id+"F0.wireOp",EDGE,"E44");var subQ1=sQuery(id+"F0.wireOp",EDGE,"E2");var subQ2=makeQuery(id+"F0.imprint","INTERSECT",VERTEX,{"derivedFrom":[subQ1,subQ0]});Q36=makeQuery(id+"F0.imprint","IMPRINT",FACE,{"disambiguationData":[TD([[makeQuery(id+"F0.imprint","IMPRINT",EDGE,{"disambiguationData":[TD([[subQ2,-1.0]])],"derivedFrom":subQ1}),1.0]])]});}
            var Q37;
            {var subQ0=sQuery(id+"F0.wireOp",EDGE,"E41");var subQ1=sQuery(id+"F0.wireOp",EDGE,"E2");var subQ2=makeQuery(id+"F0.imprint","INTERSECT",VERTEX,{"derivedFrom":[subQ1,subQ0]});Q37=makeQuery(id+"F0.imprint","IMPRINT",FACE,{"disambiguationData":[TD([[makeQuery(id+"F0.imprint","IMPRINT",EDGE,{"disambiguationData":[TD([[subQ2,-1.0]])],"derivedFrom":subQ1}),1.0]])]});}
            var Q38;
            {var subQ0=sQuery(id+"F0.wireOp",EDGE,"E38");var subQ1=sQuery(id+"F0.wireOp",EDGE,"E2");var subQ2=makeQuery(id+"F0.imprint","INTERSECT",VERTEX,{"derivedFrom":[subQ1,subQ0]});Q38=makeQuery(id+"F0.imprint","IMPRINT",FACE,{"disambiguationData":[TD([[makeQuery(id+"F0.imprint","IMPRINT",EDGE,{"disambiguationData":[TD([[subQ2,-1.0]])],"derivedFrom":subQ1}),1.0]])]});}
            var Q39;
            Q39=makeQuery(id+"F0.imprint","IMPRINT",FACE,{"disambiguationData":[TD([[makeQuery(id+"F0.imprint","IMPRINT",EDGE,{"derivedFrom":sQuery(id+"F0.wireOp",EDGE,"E75")}),-1.0]])]});
            var Q40;
            Q40=makeQuery(id+"F0.imprint","IMPRINT",FACE,{"disambiguationData":[TD([[makeQuery(id+"F0.imprint","IMPRINT",EDGE,{"derivedFrom":sQuery(id+"F0.wireOp",EDGE,"E77")}),-1.0]])]});
            var Q41;
            Q41=makeQuery(id+"F0.imprint","IMPRINT",FACE,{"disambiguationData":[TD([[makeQuery(id+"F0.imprint","IMPRINT",EDGE,{"derivedFrom":sQuery(id+"F0.wireOp",EDGE,"E79")}),-1.0]])]});
            var Q42;
            Q42=makeQuery(id+"F0.imprint","IMPRINT",FACE,{"disambiguationData":[TD([[makeQuery(id+"F0.imprint","IMPRINT",EDGE,{"derivedFrom":sQuery(id+"F0.wireOp",EDGE,"E81")}),-1.0]])]});
            var Q43;
            Q43=makeQuery(id+"F0.imprint","IMPRINT",FACE,{"disambiguationData":[TD([[makeQuery(id+"F0.imprint","IMPRINT",EDGE,{"derivedFrom":sQuery(id+"F0.wireOp",EDGE,"E83")}),-1.0]])]});
            var Q44;
            Q44=makeQuery(id+"F0.imprint","IMPRINT",FACE,{"disambiguationData":[TD([[makeQuery(id+"F0.imprint","IMPRINT",EDGE,{"derivedFrom":sQuery(id+"F0.wireOp",EDGE,"E85")}),-1.0]])]});
            var Q45;
            Q45=makeQuery(id+"F0.imprint","IMPRINT",FACE,{"disambiguationData":[TD([[makeQuery(id+"F0.imprint","IMPRINT",EDGE,{"derivedFrom":sQuery(id+"F0.wireOp",EDGE,"E87")}),-1.0]])]});
            var Q46;
            Q46=makeQuery(id+"F0.imprint","IMPRINT",FACE,{"disambiguationData":[TD([[makeQuery(id+"F0.imprint","IMPRINT",EDGE,{"derivedFrom":sQuery(id+"F0.wireOp",EDGE,"E89")}),-1.0]])]});
            var Q47;
            Q47=makeQuery(id+"F0.imprint","IMPRINT",FACE,{"disambiguationData":[TD([[makeQuery(id+"F0.imprint","IMPRINT",EDGE,{"derivedFrom":sQuery(id+"F0.wireOp",EDGE,"E91")}),-1.0]])]});
            var Q48;
            Q48=makeQuery(id+"F0.imprint","IMPRINT",FACE,{"disambiguationData":[TD([[makeQuery(id+"F0.imprint","IMPRINT",EDGE,{"derivedFrom":sQuery(id+"F0.wireOp",EDGE,"E93")}),-1.0]])]});
            var Q49;
            Q49=makeQuery(id+"F0.imprint","IMPRINT",FACE,{"disambiguationData":[TD([[makeQuery(id+"F0.imprint","IMPRINT",EDGE,{"derivedFrom":sQuery(id+"F0.wireOp",EDGE,"E95")}),-1.0]])]});
            var Q50;
            {var subQ0=sQuery(id+"F0.wireOp",EDGE,"E97");Q50=makeQuery(id+"F0.imprint","IMPRINT",FACE,{"disambiguationData":[TD([[makeQuery(id+"F0.imprint","IMPRINT",EDGE,{"derivedFrom":subQ0}),-1.0]])]});}
            extrude(context, id + "F1", {"entities" : qUnion([Q0, Q1, Q2, Q3, Q4, Q5, Q6, Q7, Q8, Q9, Q10, Q11, Q12, Q13, Q14, Q15, Q16, Q17, Q18, Q19, Q20, Q21, Q22, Q23, Q24, Q25, Q26, Q27, Q28, Q29, Q30, Q31, Q32, Q33, Q34, Q35, Q36, Q37, Q38, Q39, Q40, Q41, Q42, Q43, Q44, Q45, Q46, Q47, Q48, Q49, Q50]), "depth" : 15 * mm});
        }
        {
            var Q0;
            Q0=makeQuery(id+"F1.opExtrude","SWEPT_FACE",FACE,{"disambiguationData":[OSD([sQuery(id+"F0.wireOp",EDGE,"E0.bottom"),sQuery(id+"F0.wireOp",EDGE,"E9"),sQuery(id+"F0.wireOp",EDGE,"E40"),sQuery(id+"F0.wireOp",EDGE,"E43"),sQuery(id+"F0.wireOp",EDGE,"E46"),sQuery(id+"F0.wireOp",EDGE,"E49"),sQuery(id+"F0.wireOp",EDGE,"E52"),sQuery(id+"F0.wireOp",EDGE,"E55"),sQuery(id+"F0.wireOp",EDGE,"E58"),sQuery(id+"F0.wireOp",EDGE,"E61"),sQuery(id+"F0.wireOp",EDGE,"E64"),sQuery(id+"F0.wireOp",EDGE,"E67"),sQuery(id+"F0.wireOp",EDGE,"E70")])]});
            var sketch = newSketch(context, id + "F2", { "sketchPlane" : qUnion([Q0])});
            skLineSegment(sketch, "E169", {"start": v(-98.6, 15) * mm, "end": v(-93.6, 15) * mm});
            skLineSegment(sketch, "E170", {"start": v(-93.6, 15) * mm, "end": v(-93.6, 0) * mm});
            skLineSegment(sketch, "E171", {"start": v(101.4, 15) * mm, "end": v(96.4, 15) * mm});
            skLineSegment(sketch, "E172", {"start": v(96.4, 15) * mm, "end": v(96.4, 0) * mm});
            skLineSegment(sketch, "E173", {"start": v(96.4, 15) * mm, "end": v(1.4, 15) * mm});
            skLineSegment(sketch, "E174", {"start": v(1.4, 15) * mm, "end": v(1.4, 0) * mm});
            skLineSegment(sketch, "E175", {"start": v(1.4, 0) * mm, "end": v(4.4, 0) * mm});
            skLineSegment(sketch, "E176", {"start": v(4.4, 0) * mm, "end": v(-1.6, 0) * mm});
            skLineSegment(sketch, "E177", {"start": v(-1.6, 0) * mm, "end": v(-1.6, 15) * mm});
            skLineSegment(sketch, "E178", {"start": v(-1.6, 15) * mm, "end": v(4.4, 15) * mm});
            skLineSegment(sketch, "E179", {"start": v(4.4, 15) * mm, "end": v(4.4, 0) * mm});
            skSolve(sketch);
        }
        {
            var Q0;
            Q0=makeQuery(id+"F2.imprint","IMPRINT",FACE,{"disambiguationData":[TD([[makeQuery(id+"F2.imprint","IMPRINT",EDGE,{"derivedFrom":sQuery(id+"F2.wireOp",EDGE,"E169")}),1.0]])]});
            var Q1;
            {var subQ0=sQuery(id+"F2.wireOp",EDGE,"E174");Q1=makeQuery(id+"F2.imprint","IMPRINT",FACE,{"disambiguationData":[TD([[makeQuery(id+"F2.imprint","IMPRINT",EDGE,{"derivedFrom":subQ0}),-1.0]])]});}
            var Q2;
            {var subQ0=sQuery(id+"F2.wireOp",EDGE,"E174");Q2=makeQuery(id+"F2.imprint","IMPRINT",FACE,{"disambiguationData":[TD([[makeQuery(id+"F2.imprint","IMPRINT",EDGE,{"derivedFrom":subQ0}),1.0]])]});}
            var Q3;
            Q3=makeQuery(id+"F2.imprint","IMPRINT",FACE,{"disambiguationData":[TD([[makeQuery(id+"F2.imprint","IMPRINT",EDGE,{"derivedFrom":sQuery(id+"F2.wireOp",EDGE,"E171")}),1.0]])]});
            extrude(context, id + "F3", {"entities" : qUnion([Q0, Q1, Q2, Q3]), "operationType" : NewBodyOperationType.ADD, "depth" : 14 * mm});
        }
        {
            var Q0;
            Q0=makeQuery(id+"F3.boolean.opBoolean","MERGE",FACE,{"derivedFrom":[makeQuery(id+"F1.opExtrude","CAP_FACE",FACE,{"disambiguationData":[OSD([sQuery(id+"F0.wireOp",EDGE,"E0.bottom"),sQuery(id+"F0.wireOp",EDGE,"E0.top"),sQuery(id+"F0.wireOp",EDGE,"E0.left"),sQuery(id+"F0.wireOp",EDGE,"E0.right"),sQuery(id+"F0.wireOp",EDGE,"E1"),sQuery(id+"F0.wireOp",EDGE,"E2"),sQuery(id+"F0.wireOp",EDGE,"E3"),sQuery(id+"F0.wireOp",EDGE,"E4"),sQuery(id+"F0.wireOp",EDGE,"E5"),sQuery(id+"F0.wireOp",EDGE,"E7"),sQuery(id+"F0.wireOp",EDGE,"E9"),sQuery(id+"F0.wireOp",EDGE,"E10"),sQuery(id+"F0.wireOp",EDGE,"E11"),sQuery(id+"F0.wireOp",EDGE,"E12"),sQuery(id+"F0.wireOp",EDGE,"E13"),sQuery(id+"F0.wireOp",EDGE,"E14"),sQuery(id+"F0.wireOp",EDGE,"E15"),sQuery(id+"F0.wireOp",EDGE,"E16"),sQuery(id+"F0.wireOp",EDGE,"E17"),sQuery(id+"F0.wireOp",EDGE,"E18"),sQuery(id+"F0.wireOp",EDGE,"E19"),sQuery(id+"F0.wireOp",EDGE,"E20"),sQuery(id+"F0.wireOp",EDGE,"E21"),sQuery(id+"F0.wireOp",EDGE,"E22"),sQuery(id+"F0.wireOp",EDGE,"E23"),sQuery(id+"F0.wireOp",EDGE,"E24"),sQuery(id+"F0.wireOp",EDGE,"E25"),sQuery(id+"F0.wireOp",EDGE,"E26"),sQuery(id+"F0.wireOp",EDGE,"E27"),sQuery(id+"F0.wireOp",EDGE,"E28"),sQuery(id+"F0.wireOp",EDGE,"E29"),sQuery(id+"F0.wireOp",EDGE,"E30"),sQuery(id+"F0.wireOp",EDGE,"E31"),sQuery(id+"F0.wireOp",EDGE,"E32"),sQuery(id+"F0.wireOp",EDGE,"E33"),sQuery(id+"F0.wireOp",EDGE,"E34"),sQuery(id+"F0.wireOp",EDGE,"E35"),sQuery(id+"F0.wireOp",EDGE,"E36"),sQuery(id+"F0.wireOp",EDGE,"E37"),sQuery(id+"F0.wireOp",EDGE,"E38"),sQuery(id+"F0.wireOp",EDGE,"E39"),sQuery(id+"F0.wireOp",EDGE,"E40"),sQuery(id+"F0.wireOp",EDGE,"E41"),sQuery(id+"F0.wireOp",EDGE,"E42"),sQuery(id+"F0.wireOp",EDGE,"E43"),sQuery(id+"F0.wireOp",EDGE,"E44"),sQuery(id+"F0.wireOp",EDGE,"E45"),sQuery(id+"F0.wireOp",EDGE,"E46"),sQuery(id+"F0.wireOp",EDGE,"E47"),sQuery(id+"F0.wireOp",EDGE,"E48"),sQuery(id+"F0.wireOp",EDGE,"E49"),sQuery(id+"F0.wireOp",EDGE,"E50"),sQuery(id+"F0.wireOp",EDGE,"E51"),sQuery(id+"F0.wireOp",EDGE,"E52"),sQuery(id+"F0.wireOp",EDGE,"E53"),sQuery(id+"F0.wireOp",EDGE,"E54"),sQuery(id+"F0.wireOp",EDGE,"E55"),sQuery(id+"F0.wireOp",EDGE,"E56"),sQuery(id+"F0.wireOp",EDGE,"E57"),sQuery(id+"F0.wireOp",EDGE,"E58"),sQuery(id+"F0.wireOp",EDGE,"E59"),sQuery(id+"F0.wireOp",EDGE,"E60"),sQuery(id+"F0.wireOp",EDGE,"E61"),sQuery(id+"F0.wireOp",EDGE,"E62"),sQuery(id+"F0.wireOp",EDGE,"E63"),sQuery(id+"F0.wireOp",EDGE,"E64"),sQuery(id+"F0.wireOp",EDGE,"E65"),sQuery(id+"F0.wireOp",EDGE,"E66"),sQuery(id+"F0.wireOp",EDGE,"E67"),sQuery(id+"F0.wireOp",EDGE,"E68"),sQuery(id+"F0.wireOp",EDGE,"E69"),sQuery(id+"F0.wireOp",EDGE,"E70"),sQuery(id+"F0.wireOp",EDGE,"E71"),sQuery(id+"F0.wireOp",EDGE,"E72"),sQuery(id+"F0.wireOp",EDGE,"E74"),sQuery(id+"F0.wireOp",EDGE,"E76"),sQuery(id+"F0.wireOp",EDGE,"E78"),sQuery(id+"F0.wireOp",EDGE,"E80"),sQuery(id+"F0.wireOp",EDGE,"E82"),sQuery(id+"F0.wireOp",EDGE,"E84"),sQuery(id+"F0.wireOp",EDGE,"E86"),sQuery(id+"F0.wireOp",EDGE,"E88"),sQuery(id+"F0.wireOp",EDGE,"E90"),sQuery(id+"F0.wireOp",EDGE,"E92"),sQuery(id+"F0.wireOp",EDGE,"E94"),sQuery(id+"F0.wireOp",EDGE,"E96"),sQuery(id+"F0.wireOp",EDGE,"E98"),sQuery(id+"F0.wireOp",EDGE,"E99"),sQuery(id+"F0.wireOp",EDGE,"E100"),sQuery(id+"F0.wireOp",EDGE,"E101"),sQuery(id+"F0.wireOp",EDGE,"E102"),sQuery(id+"F0.wireOp",EDGE,"E103"),sQuery(id+"F0.wireOp",EDGE,"E104"),sQuery(id+"F0.wireOp",EDGE,"E105"),sQuery(id+"F0.wireOp",EDGE,"E106"),sQuery(id+"F0.wireOp",EDGE,"E107"),sQuery(id+"F0.wireOp",EDGE,"E108"),sQuery(id+"F0.wireOp",EDGE,"E109"),sQuery(id+"F0.wireOp",EDGE,"E110"),sQuery(id+"F0.wireOp",EDGE,"E111"),sQuery(id+"F0.wireOp",EDGE,"E112"),sQuery(id+"F0.wireOp",EDGE,"E113"),sQuery(id+"F0.wireOp",EDGE,"E114"),sQuery(id+"F0.wireOp",EDGE,"E115"),sQuery(id+"F0.wireOp",EDGE,"E116"),sQuery(id+"F0.wireOp",EDGE,"E117"),sQuery(id+"F0.wireOp",EDGE,"E118"),sQuery(id+"F0.wireOp",EDGE,"E119"),sQuery(id+"F0.wireOp",EDGE,"E120"),sQuery(id+"F0.wireOp",EDGE,"E121"),sQuery(id+"F0.wireOp",EDGE,"E122"),sQuery(id+"F0.wireOp",EDGE,"E123"),sQuery(id+"F0.wireOp",EDGE,"E124"),sQuery(id+"F0.wireOp",EDGE,"E125"),sQuery(id+"F0.wireOp",EDGE,"E126"),sQuery(id+"F0.wireOp",EDGE,"E127"),sQuery(id+"F0.wireOp",EDGE,"E128"),sQuery(id+"F0.wireOp",EDGE,"E129"),sQuery(id+"F0.wireOp",EDGE,"E130"),sQuery(id+"F0.wireOp",EDGE,"E131"),sQuery(id+"F0.wireOp",EDGE,"E132"),sQuery(id+"F0.wireOp",EDGE,"E133"),sQuery(id+"F0.wireOp",EDGE,"E136"),sQuery(id+"F0.wireOp",EDGE,"E147"),sQuery(id+"F0.wireOp",EDGE,"E158"),sQuery(id+"F0.wireOp",EDGE,"E159"),sQuery(id+"F0.wireOp",EDGE,"E160"),sQuery(id+"F0.wireOp",EDGE,"E161"),sQuery(id+"F0.wireOp",EDGE,"E162"),sQuery(id+"F0.wireOp",EDGE,"E163"),sQuery(id+"F0.wireOp",EDGE,"E164"),sQuery(id+"F0.wireOp",EDGE,"E165"),sQuery(id+"F0.wireOp",EDGE,"E166"),sQuery(id+"F0.wireOp",EDGE,"E167"),sQuery(id+"F0.wireOp",EDGE,"E168")])],"isStart":false}),makeQuery(id+"F3.opExtrude","SWEPT_FACE",FACE,{"disambiguationData":[OSD([sQuery(id+"F2.wireOp",EDGE,"E169")])]}),makeQuery(id+"F3.opExtrude","SWEPT_FACE",FACE,{"disambiguationData":[OSD([sQuery(id+"F2.wireOp",EDGE,"E171")])]}),makeQuery(id+"F3.opExtrude","SWEPT_FACE",FACE,{"disambiguationData":[OSD([sQuery(id+"F2.wireOp",EDGE,"E178")])]})]});
            var sketch = newSketch(context, id + "F4", { "sketchPlane" : qUnion([Q0])});
            skLineSegment(sketch, "E180", {"start": v(98.6, 2.85) * mm, "end": v(98.6, -1.15) * mm});
            skLineSegment(sketch, "E181", {"start": v(98.6, -1.15) * mm, "end": v(-101.4, -1.15) * mm});
            skLineSegment(sketch, "E182", {"start": v(-101.4, -1.15) * mm, "end": v(-101.4, 2.85) * mm});
            skLineSegment(sketch, "E183", {"start": v(-101.4, 2.85) * mm, "end": v(98.6, 2.85) * mm});
            skSolve(sketch);
        }
        {
            var Q0;
            {var subQ0=sQuery(id+"F4.wireOp",EDGE,"E180");Q0=makeQuery(id+"F4.imprint","IMPRINT",FACE,{"disambiguationData":[TD([[makeQuery(id+"F4.imprint","IMPRINT",EDGE,{"derivedFrom":subQ0}),-1.0]])]});}
            var Q1;
            {var subQ0=sQuery(id+"F4.wireOp",EDGE,"E181");var subQ1=sQuery(id+"F0.wireOp",EDGE,"E70");var subQ2=sQuery(id+"F0.wireOp",EDGE,"E67");var subQ3=sQuery(id+"F0.wireOp",EDGE,"E64");var subQ4=sQuery(id+"F0.wireOp",EDGE,"E61");var subQ5=sQuery(id+"F0.wireOp",EDGE,"E58");var subQ6=sQuery(id+"F0.wireOp",EDGE,"E55");var subQ7=sQuery(id+"F0.wireOp",EDGE,"E52");var subQ8=sQuery(id+"F0.wireOp",EDGE,"E49");var subQ9=sQuery(id+"F0.wireOp",EDGE,"E46");var subQ10=sQuery(id+"F0.wireOp",EDGE,"E43");var subQ11=sQuery(id+"F0.wireOp",EDGE,"E40");var subQ12=sQuery(id+"F0.wireOp",EDGE,"E9");var subQ13=sQuery(id+"F0.wireOp",EDGE,"E0.bottom");var subQ14=makeQuery(id+"F3.opExtrude","SWEPT_EDGE",EDGE,{"disambiguationData":[OSD([subQ13,subQ12,subQ11,subQ10,subQ9,subQ8,subQ7,subQ6,subQ5,subQ4,subQ3,subQ2,subQ1,sQuery(id+"F2.wireOp",EDGE,"E169"),sQuery(id+"F2.wireOp",EDGE,"E170")])]});var subQ15=makeQuery(id+"F4.imprint","INTERSECT",VERTEX,{"derivedFrom":[subQ14,subQ0]});Q1=makeQuery(id+"F4.imprint","IMPRINT",FACE,{"disambiguationData":[TD([[makeQuery(id+"F4.imprint","IMPRINT",EDGE,{"disambiguationData":[TD([[subQ15,-1.0]])],"derivedFrom":subQ0}),-1.0]])]});}
            var Q2;
            {var subQ1=sQuery(id+"F2.wireOp",EDGE,"E178");var subQ4=makeQuery(id+"F3.opExtrude","SWEPT_EDGE",EDGE,{"disambiguationData":[OSD([sQuery(id+"F2.wireOp",EDGE,"E173"),subQ1,sQuery(id+"F2.wireOp",EDGE,"E179")])]});var subQ6=sQuery(id+"F4.wireOp",EDGE,"E183");var subQ7=makeQuery(id+"F4.imprint","INTERSECT",VERTEX,{"derivedFrom":[subQ4,subQ6]});Q2=makeQuery(id+"F4.imprint","IMPRINT",FACE,{"disambiguationData":[TD([[makeQuery(id+"F4.imprint","IMPRINT",EDGE,{"disambiguationData":[TD([[subQ7,-1.0]])],"derivedFrom":subQ4}),1.0]])]});}
            var Q3;
            {var subQ0=sQuery(id+"F4.wireOp",EDGE,"E181");var subQ1=sQuery(id+"F2.wireOp",EDGE,"E173");var subQ2=makeQuery(id+"F3.opExtrude","SWEPT_EDGE",EDGE,{"disambiguationData":[OSD([subQ1,sQuery(id+"F2.wireOp",EDGE,"E178"),sQuery(id+"F2.wireOp",EDGE,"E179")])]});var subQ3=makeQuery(id+"F4.imprint","INTERSECT",VERTEX,{"derivedFrom":[subQ2,subQ0]});Q3=makeQuery(id+"F4.imprint","IMPRINT",FACE,{"disambiguationData":[TD([[makeQuery(id+"F4.imprint","IMPRINT",EDGE,{"disambiguationData":[TD([[subQ3,-1.0]])],"derivedFrom":subQ0}),-1.0]])]});}
            var Q4;
            {var subQ0=sQuery(id+"F4.wireOp",EDGE,"E182");Q4=makeQuery(id+"F4.imprint","IMPRINT",FACE,{"disambiguationData":[TD([[makeQuery(id+"F4.imprint","IMPRINT",EDGE,{"derivedFrom":subQ0}),-1.0]])]});}
            extrude(context, id + "F5", {"entities" : qUnion([Q0, Q1, Q2, Q3, Q4]), "operationType" : NewBodyOperationType.ADD, "depth" : 15 * mm, "hasSecondDirection" : true, "secondDirectionOppositeDirection" : true, "secondDirectionDepth" : 15 * mm});
        }
        {
            var Q0;
            Q0=makeQuery(id+"F5.opExtrude","SWEPT_FACE",FACE,{"disambiguationData":[OSD([sQuery(id+"F4.wireOp",EDGE,"E181")])]});
            var sketch = newSketch(context, id + "F6", { "sketchPlane" : qUnion([Q0])});
            skLineSegment(sketch, "E184", {"start": v(-101.4, 30) * mm, "end": v(-101.4, 22.5) * mm});
            skLineSegment(sketch, "E185", {"start": v(-101.4, 22.5) * mm, "end": v(98.6, 22.5) * mm});
            skLineSegment(sketch, "E186", {"start": v(98.6, 22.5) * mm, "end": v(-1.4, 22.5) * mm});
            skPoint(sketch, "E186.endSnap0", {"position": v(-1.4, 15) * mm});
            skLineSegment(sketch, "E187", {"start": v(-1.4, 22.5) * mm, "end": v(82.52, 22.5) * mm});
            skLineSegment(sketch, "E188", {"start": v(82.52, 22.5) * mm, "end": v(-84.93, 22.5) * mm});
            skSolve(sketch);
        }
        {
            var Q0;
            Q0=sQuery(id+"F6.wireOp",VERTEX,"E187.start");
            var Q1;
            Q1=sQuery(id+"F6.wireOp",VERTEX,"E187.end");
            var Q2;
            Q2=sQuery(id+"F6.wireOp",VERTEX,"E188.end");
            var Q3;
            Q3=makeQuery(id+"F1.opExtrude","SWEPT_BODY",BODY,{"disambiguationData":[OSD([sQuery(id+"F0.wireOp",EDGE,"E0.bottom"),sQuery(id+"F0.wireOp",EDGE,"E0.top"),sQuery(id+"F0.wireOp",EDGE,"E0.left"),sQuery(id+"F0.wireOp",EDGE,"E0.right"),sQuery(id+"F0.wireOp",EDGE,"E1"),sQuery(id+"F0.wireOp",EDGE,"E2"),sQuery(id+"F0.wireOp",EDGE,"E3"),sQuery(id+"F0.wireOp",EDGE,"E4"),sQuery(id+"F0.wireOp",EDGE,"E5"),sQuery(id+"F0.wireOp",EDGE,"E7"),sQuery(id+"F0.wireOp",EDGE,"E9"),sQuery(id+"F0.wireOp",EDGE,"E10"),sQuery(id+"F0.wireOp",EDGE,"E11"),sQuery(id+"F0.wireOp",EDGE,"E12"),sQuery(id+"F0.wireOp",EDGE,"E13"),sQuery(id+"F0.wireOp",EDGE,"E14"),sQuery(id+"F0.wireOp",EDGE,"E15"),sQuery(id+"F0.wireOp",EDGE,"E16"),sQuery(id+"F0.wireOp",EDGE,"E17"),sQuery(id+"F0.wireOp",EDGE,"E18"),sQuery(id+"F0.wireOp",EDGE,"E19"),sQuery(id+"F0.wireOp",EDGE,"E20"),sQuery(id+"F0.wireOp",EDGE,"E21"),sQuery(id+"F0.wireOp",EDGE,"E22"),sQuery(id+"F0.wireOp",EDGE,"E23"),sQuery(id+"F0.wireOp",EDGE,"E24"),sQuery(id+"F0.wireOp",EDGE,"E25"),sQuery(id+"F0.wireOp",EDGE,"E26"),sQuery(id+"F0.wireOp",EDGE,"E27"),sQuery(id+"F0.wireOp",EDGE,"E28"),sQuery(id+"F0.wireOp",EDGE,"E29"),sQuery(id+"F0.wireOp",EDGE,"E30"),sQuery(id+"F0.wireOp",EDGE,"E31"),sQuery(id+"F0.wireOp",EDGE,"E32"),sQuery(id+"F0.wireOp",EDGE,"E33"),sQuery(id+"F0.wireOp",EDGE,"E34"),sQuery(id+"F0.wireOp",EDGE,"E35"),sQuery(id+"F0.wireOp",EDGE,"E36"),sQuery(id+"F0.wireOp",EDGE,"E37"),sQuery(id+"F0.wireOp",EDGE,"E38"),sQuery(id+"F0.wireOp",EDGE,"E39"),sQuery(id+"F0.wireOp",EDGE,"E40"),sQuery(id+"F0.wireOp",EDGE,"E41"),sQuery(id+"F0.wireOp",EDGE,"E42"),sQuery(id+"F0.wireOp",EDGE,"E43"),sQuery(id+"F0.wireOp",EDGE,"E44"),sQuery(id+"F0.wireOp",EDGE,"E45"),sQuery(id+"F0.wireOp",EDGE,"E46"),sQuery(id+"F0.wireOp",EDGE,"E47"),sQuery(id+"F0.wireOp",EDGE,"E48"),sQuery(id+"F0.wireOp",EDGE,"E49"),sQuery(id+"F0.wireOp",EDGE,"E50"),sQuery(id+"F0.wireOp",EDGE,"E51"),sQuery(id+"F0.wireOp",EDGE,"E52"),sQuery(id+"F0.wireOp",EDGE,"E53"),sQuery(id+"F0.wireOp",EDGE,"E54"),sQuery(id+"F0.wireOp",EDGE,"E55"),sQuery(id+"F0.wireOp",EDGE,"E56"),sQuery(id+"F0.wireOp",EDGE,"E57"),sQuery(id+"F0.wireOp",EDGE,"E58"),sQuery(id+"F0.wireOp",EDGE,"E59"),sQuery(id+"F0.wireOp",EDGE,"E60"),sQuery(id+"F0.wireOp",EDGE,"E61"),sQuery(id+"F0.wireOp",EDGE,"E62"),sQuery(id+"F0.wireOp",EDGE,"E63"),sQuery(id+"F0.wireOp",EDGE,"E64"),sQuery(id+"F0.wireOp",EDGE,"E65"),sQuery(id+"F0.wireOp",EDGE,"E66"),sQuery(id+"F0.wireOp",EDGE,"E67"),sQuery(id+"F0.wireOp",EDGE,"E68"),sQuery(id+"F0.wireOp",EDGE,"E69"),sQuery(id+"F0.wireOp",EDGE,"E70"),sQuery(id+"F0.wireOp",EDGE,"E71"),sQuery(id+"F0.wireOp",EDGE,"E72"),sQuery(id+"F0.wireOp",EDGE,"E74"),sQuery(id+"F0.wireOp",EDGE,"E76"),sQuery(id+"F0.wireOp",EDGE,"E78"),sQuery(id+"F0.wireOp",EDGE,"E80"),sQuery(id+"F0.wireOp",EDGE,"E82"),sQuery(id+"F0.wireOp",EDGE,"E84"),sQuery(id+"F0.wireOp",EDGE,"E86"),sQuery(id+"F0.wireOp",EDGE,"E88"),sQuery(id+"F0.wireOp",EDGE,"E90"),sQuery(id+"F0.wireOp",EDGE,"E92"),sQuery(id+"F0.wireOp",EDGE,"E94"),sQuery(id+"F0.wireOp",EDGE,"E96"),sQuery(id+"F0.wireOp",EDGE,"E98"),sQuery(id+"F0.wireOp",EDGE,"E99"),sQuery(id+"F0.wireOp",EDGE,"E100"),sQuery(id+"F0.wireOp",EDGE,"E101"),sQuery(id+"F0.wireOp",EDGE,"E102"),sQuery(id+"F0.wireOp",EDGE,"E103"),sQuery(id+"F0.wireOp",EDGE,"E104"),sQuery(id+"F0.wireOp",EDGE,"E105"),sQuery(id+"F0.wireOp",EDGE,"E106"),sQuery(id+"F0.wireOp",EDGE,"E107"),sQuery(id+"F0.wireOp",EDGE,"E108"),sQuery(id+"F0.wireOp",EDGE,"E109"),sQuery(id+"F0.wireOp",EDGE,"E110"),sQuery(id+"F0.wireOp",EDGE,"E111"),sQuery(id+"F0.wireOp",EDGE,"E112"),sQuery(id+"F0.wireOp",EDGE,"E113"),sQuery(id+"F0.wireOp",EDGE,"E114"),sQuery(id+"F0.wireOp",EDGE,"E115"),sQuery(id+"F0.wireOp",EDGE,"E116"),sQuery(id+"F0.wireOp",EDGE,"E117"),sQuery(id+"F0.wireOp",EDGE,"E118"),sQuery(id+"F0.wireOp",EDGE,"E119"),sQuery(id+"F0.wireOp",EDGE,"E120"),sQuery(id+"F0.wireOp",EDGE,"E121"),sQuery(id+"F0.wireOp",EDGE,"E122"),sQuery(id+"F0.wireOp",EDGE,"E123"),sQuery(id+"F0.wireOp",EDGE,"E124"),sQuery(id+"F0.wireOp",EDGE,"E125"),sQuery(id+"F0.wireOp",EDGE,"E126"),sQuery(id+"F0.wireOp",EDGE,"E127"),sQuery(id+"F0.wireOp",EDGE,"E128"),sQuery(id+"F0.wireOp",EDGE,"E129"),sQuery(id+"F0.wireOp",EDGE,"E130"),sQuery(id+"F0.wireOp",EDGE,"E131"),sQuery(id+"F0.wireOp",EDGE,"E132"),sQuery(id+"F0.wireOp",EDGE,"E133"),sQuery(id+"F0.wireOp",EDGE,"E136"),sQuery(id+"F0.wireOp",EDGE,"E147"),sQuery(id+"F0.wireOp",EDGE,"E158"),sQuery(id+"F0.wireOp",EDGE,"E159"),sQuery(id+"F0.wireOp",EDGE,"E160"),sQuery(id+"F0.wireOp",EDGE,"E161"),sQuery(id+"F0.wireOp",EDGE,"E162"),sQuery(id+"F0.wireOp",EDGE,"E163"),sQuery(id+"F0.wireOp",EDGE,"E164"),sQuery(id+"F0.wireOp",EDGE,"E165"),sQuery(id+"F0.wireOp",EDGE,"E166"),sQuery(id+"F0.wireOp",EDGE,"E167"),sQuery(id+"F0.wireOp",EDGE,"E168")])]});
            hole(context, id + "F7", {"style" : HoleStyle.C_SINK, "endStyle" : HoleEndStyle.BLIND, "holeDiameter" : 5 * mm, "cSinkDiameter" : 9.5 * mm, "cSinkAngle" : 60 * degree, "holeDepth" : 20 * mm, "isTappedThrough" : true, "tappedDepth" : 12.7 * mm, "tapClearance" : 3, "locations" : qUnion([Q0, Q1, Q2]), "scope" : qUnion([Q3])});
        }
        {
            var Q0;
            Q0=makeQuery(id+"F3.boolean.opBoolean","MERGE",FACE,{"derivedFrom":[makeQuery(id+"F1.opExtrude","CAP_FACE",FACE,{"disambiguationData":[OSD([sQuery(id+"F0.wireOp",EDGE,"E0.bottom"),sQuery(id+"F0.wireOp",EDGE,"E0.top"),sQuery(id+"F0.wireOp",EDGE,"E0.left"),sQuery(id+"F0.wireOp",EDGE,"E0.right"),sQuery(id+"F0.wireOp",EDGE,"E1"),sQuery(id+"F0.wireOp",EDGE,"E2"),sQuery(id+"F0.wireOp",EDGE,"E3"),sQuery(id+"F0.wireOp",EDGE,"E4"),sQuery(id+"F0.wireOp",EDGE,"E5"),sQuery(id+"F0.wireOp",EDGE,"E7"),sQuery(id+"F0.wireOp",EDGE,"E9"),sQuery(id+"F0.wireOp",EDGE,"E10"),sQuery(id+"F0.wireOp",EDGE,"E11"),sQuery(id+"F0.wireOp",EDGE,"E12"),sQuery(id+"F0.wireOp",EDGE,"E13"),sQuery(id+"F0.wireOp",EDGE,"E14"),sQuery(id+"F0.wireOp",EDGE,"E15"),sQuery(id+"F0.wireOp",EDGE,"E16"),sQuery(id+"F0.wireOp",EDGE,"E17"),sQuery(id+"F0.wireOp",EDGE,"E18"),sQuery(id+"F0.wireOp",EDGE,"E19"),sQuery(id+"F0.wireOp",EDGE,"E20"),sQuery(id+"F0.wireOp",EDGE,"E21"),sQuery(id+"F0.wireOp",EDGE,"E22"),sQuery(id+"F0.wireOp",EDGE,"E23"),sQuery(id+"F0.wireOp",EDGE,"E24"),sQuery(id+"F0.wireOp",EDGE,"E25"),sQuery(id+"F0.wireOp",EDGE,"E26"),sQuery(id+"F0.wireOp",EDGE,"E27"),sQuery(id+"F0.wireOp",EDGE,"E28"),sQuery(id+"F0.wireOp",EDGE,"E29"),sQuery(id+"F0.wireOp",EDGE,"E30"),sQuery(id+"F0.wireOp",EDGE,"E31"),sQuery(id+"F0.wireOp",EDGE,"E32"),sQuery(id+"F0.wireOp",EDGE,"E33"),sQuery(id+"F0.wireOp",EDGE,"E34"),sQuery(id+"F0.wireOp",EDGE,"E35"),sQuery(id+"F0.wireOp",EDGE,"E36"),sQuery(id+"F0.wireOp",EDGE,"E37"),sQuery(id+"F0.wireOp",EDGE,"E38"),sQuery(id+"F0.wireOp",EDGE,"E39"),sQuery(id+"F0.wireOp",EDGE,"E40"),sQuery(id+"F0.wireOp",EDGE,"E41"),sQuery(id+"F0.wireOp",EDGE,"E42"),sQuery(id+"F0.wireOp",EDGE,"E43"),sQuery(id+"F0.wireOp",EDGE,"E44"),sQuery(id+"F0.wireOp",EDGE,"E45"),sQuery(id+"F0.wireOp",EDGE,"E46"),sQuery(id+"F0.wireOp",EDGE,"E47"),sQuery(id+"F0.wireOp",EDGE,"E48"),sQuery(id+"F0.wireOp",EDGE,"E49"),sQuery(id+"F0.wireOp",EDGE,"E50"),sQuery(id+"F0.wireOp",EDGE,"E51"),sQuery(id+"F0.wireOp",EDGE,"E52"),sQuery(id+"F0.wireOp",EDGE,"E53"),sQuery(id+"F0.wireOp",EDGE,"E54"),sQuery(id+"F0.wireOp",EDGE,"E55"),sQuery(id+"F0.wireOp",EDGE,"E56"),sQuery(id+"F0.wireOp",EDGE,"E57"),sQuery(id+"F0.wireOp",EDGE,"E58"),sQuery(id+"F0.wireOp",EDGE,"E59"),sQuery(id+"F0.wireOp",EDGE,"E60"),sQuery(id+"F0.wireOp",EDGE,"E61"),sQuery(id+"F0.wireOp",EDGE,"E62"),sQuery(id+"F0.wireOp",EDGE,"E63"),sQuery(id+"F0.wireOp",EDGE,"E64"),sQuery(id+"F0.wireOp",EDGE,"E65"),sQuery(id+"F0.wireOp",EDGE,"E66"),sQuery(id+"F0.wireOp",EDGE,"E67"),sQuery(id+"F0.wireOp",EDGE,"E68"),sQuery(id+"F0.wireOp",EDGE,"E69"),sQuery(id+"F0.wireOp",EDGE,"E70"),sQuery(id+"F0.wireOp",EDGE,"E71"),sQuery(id+"F0.wireOp",EDGE,"E72"),sQuery(id+"F0.wireOp",EDGE,"E74"),sQuery(id+"F0.wireOp",EDGE,"E76"),sQuery(id+"F0.wireOp",EDGE,"E78"),sQuery(id+"F0.wireOp",EDGE,"E80"),sQuery(id+"F0.wireOp",EDGE,"E82"),sQuery(id+"F0.wireOp",EDGE,"E84"),sQuery(id+"F0.wireOp",EDGE,"E86"),sQuery(id+"F0.wireOp",EDGE,"E88"),sQuery(id+"F0.wireOp",EDGE,"E90"),sQuery(id+"F0.wireOp",EDGE,"E92"),sQuery(id+"F0.wireOp",EDGE,"E94"),sQuery(id+"F0.wireOp",EDGE,"E96"),sQuery(id+"F0.wireOp",EDGE,"E98"),sQuery(id+"F0.wireOp",EDGE,"E99"),sQuery(id+"F0.wireOp",EDGE,"E100"),sQuery(id+"F0.wireOp",EDGE,"E101"),sQuery(id+"F0.wireOp",EDGE,"E102"),sQuery(id+"F0.wireOp",EDGE,"E103"),sQuery(id+"F0.wireOp",EDGE,"E104"),sQuery(id+"F0.wireOp",EDGE,"E105"),sQuery(id+"F0.wireOp",EDGE,"E106"),sQuery(id+"F0.wireOp",EDGE,"E107"),sQuery(id+"F0.wireOp",EDGE,"E108"),sQuery(id+"F0.wireOp",EDGE,"E109"),sQuery(id+"F0.wireOp",EDGE,"E110"),sQuery(id+"F0.wireOp",EDGE,"E111"),sQuery(id+"F0.wireOp",EDGE,"E112"),sQuery(id+"F0.wireOp",EDGE,"E113"),sQuery(id+"F0.wireOp",EDGE,"E114"),sQuery(id+"F0.wireOp",EDGE,"E115"),sQuery(id+"F0.wireOp",EDGE,"E116"),sQuery(id+"F0.wireOp",EDGE,"E117"),sQuery(id+"F0.wireOp",EDGE,"E118"),sQuery(id+"F0.wireOp",EDGE,"E119"),sQuery(id+"F0.wireOp",EDGE,"E120"),sQuery(id+"F0.wireOp",EDGE,"E121"),sQuery(id+"F0.wireOp",EDGE,"E122"),sQuery(id+"F0.wireOp",EDGE,"E123"),sQuery(id+"F0.wireOp",EDGE,"E124"),sQuery(id+"F0.wireOp",EDGE,"E125"),sQuery(id+"F0.wireOp",EDGE,"E126"),sQuery(id+"F0.wireOp",EDGE,"E127"),sQuery(id+"F0.wireOp",EDGE,"E128"),sQuery(id+"F0.wireOp",EDGE,"E129"),sQuery(id+"F0.wireOp",EDGE,"E130"),sQuery(id+"F0.wireOp",EDGE,"E131"),sQuery(id+"F0.wireOp",EDGE,"E132"),sQuery(id+"F0.wireOp",EDGE,"E133"),sQuery(id+"F0.wireOp",EDGE,"E136"),sQuery(id+"F0.wireOp",EDGE,"E147"),sQuery(id+"F0.wireOp",EDGE,"E158"),sQuery(id+"F0.wireOp",EDGE,"E159"),sQuery(id+"F0.wireOp",EDGE,"E160"),sQuery(id+"F0.wireOp",EDGE,"E161"),sQuery(id+"F0.wireOp",EDGE,"E162"),sQuery(id+"F0.wireOp",EDGE,"E163"),sQuery(id+"F0.wireOp",EDGE,"E164"),sQuery(id+"F0.wireOp",EDGE,"E165"),sQuery(id+"F0.wireOp",EDGE,"E166"),sQuery(id+"F0.wireOp",EDGE,"E167"),sQuery(id+"F0.wireOp",EDGE,"E168")])],"isStart":false}),makeQuery(id+"F3.opExtrude","SWEPT_FACE",FACE,{"disambiguationData":[OSD([sQuery(id+"F2.wireOp",EDGE,"E169")])]}),makeQuery(id+"F3.opExtrude","SWEPT_FACE",FACE,{"disambiguationData":[OSD([sQuery(id+"F2.wireOp",EDGE,"E171")])]}),makeQuery(id+"F3.opExtrude","SWEPT_FACE",FACE,{"disambiguationData":[OSD([sQuery(id+"F2.wireOp",EDGE,"E178")])]})]});
            var sketch = newSketch(context, id + "F8", { "sketchPlane" : qUnion([Q0])});
            skLineSegment(sketch, "E189", {"start": v(-4.4, -11.15) * mm, "end": v(-4.4, -6.15) * mm});
            skLineSegment(sketch, "E190", {"start": v(-4.4, -6.15) * mm, "end": v(-2.9, -6.15) * mm});
            skLineSegment(sketch, "E191", {"start": v(-2.9, -6.15) * mm, "end": v(-2.9, -11.15) * mm});
            skLineSegment(sketch, "E192", {"start": v(-2.9, -11.15) * mm, "end": v(-4.4, -11.15) * mm});
            skLineSegment(sketch, "E193", {"start": v(1.6, -6.15) * mm, "end": v(0.1, -6.15) * mm});
            skPoint(sketch, "E193.endSnap0", {"position": v(1.6, -6.15) * mm});
            skLineSegment(sketch, "E194", {"start": v(0.1, -6.15) * mm, "end": v(0.1, -11.15) * mm});
            skLineSegment(sketch, "E195", {"start": v(0.1, -11.15) * mm, "end": v(1.6, -11.15) * mm});
            skSolve(sketch);
        }
        {
            var Q0;
            Q0=makeQuery(id+"F8.imprint","IMPRINT",FACE,{"disambiguationData":[TD([[makeQuery(id+"F8.imprint","IMPRINT",EDGE,{"derivedFrom":sQuery(id+"F8.wireOp",EDGE,"E189")}),1.0]])]});
            var Q1;
            {var subQ0=sQuery(id+"F8.wireOp",EDGE,"E193");Q1=makeQuery(id+"F8.imprint","IMPRINT",FACE,{"disambiguationData":[TD([[makeQuery(id+"F8.imprint","IMPRINT",EDGE,{"derivedFrom":subQ0}),1.0]])]});}
            extrude(context, id + "F9", {"entities" : qUnion([Q0, Q1]), "operationType" : NewBodyOperationType.REMOVE, "oppositeDirection" : true, "depth" : 15 * mm});
        }
        {
            var Q0;
            Q0=makeQuery(id+"F1.opExtrude","CAP_EDGE",EDGE,{"disambiguationData":[OSD([sQuery(id+"F0.wireOp",EDGE,"E0.top"),sQuery(id+"F0.wireOp",EDGE,"E11"),sQuery(id+"F0.wireOp",EDGE,"E12"),sQuery(id+"F0.wireOp",EDGE,"E13"),sQuery(id+"F0.wireOp",EDGE,"E14"),sQuery(id+"F0.wireOp",EDGE,"E15"),sQuery(id+"F0.wireOp",EDGE,"E16"),sQuery(id+"F0.wireOp",EDGE,"E17"),sQuery(id+"F0.wireOp",EDGE,"E18"),sQuery(id+"F0.wireOp",EDGE,"E19"),sQuery(id+"F0.wireOp",EDGE,"E20"),sQuery(id+"F0.wireOp",EDGE,"E21"),sQuery(id+"F0.wireOp",EDGE,"E22"),sQuery(id+"F0.wireOp",EDGE,"E23"),sQuery(id+"F0.wireOp",EDGE,"E24"),sQuery(id+"F0.wireOp",EDGE,"E25"),sQuery(id+"F0.wireOp",EDGE,"E26"),sQuery(id+"F0.wireOp",EDGE,"E27"),sQuery(id+"F0.wireOp",EDGE,"E28"),sQuery(id+"F0.wireOp",EDGE,"E29"),sQuery(id+"F0.wireOp",EDGE,"E30"),sQuery(id+"F0.wireOp",EDGE,"E31"),sQuery(id+"F0.wireOp",EDGE,"E32"),sQuery(id+"F0.wireOp",EDGE,"E33"),sQuery(id+"F0.wireOp",EDGE,"E34"),sQuery(id+"F0.wireOp",EDGE,"E35"),sQuery(id+"F0.wireOp",EDGE,"E36")])],"isStart":false});
            var Q1;
            {var subQ0=sQuery(id+"F0.wireOp",EDGE,"E70");var subQ1=sQuery(id+"F0.wireOp",EDGE,"E67");var subQ2=sQuery(id+"F0.wireOp",EDGE,"E64");var subQ3=sQuery(id+"F0.wireOp",EDGE,"E61");var subQ4=sQuery(id+"F0.wireOp",EDGE,"E58");var subQ5=sQuery(id+"F0.wireOp",EDGE,"E55");var subQ6=sQuery(id+"F0.wireOp",EDGE,"E52");var subQ7=sQuery(id+"F0.wireOp",EDGE,"E49");var subQ8=sQuery(id+"F0.wireOp",EDGE,"E46");var subQ9=sQuery(id+"F0.wireOp",EDGE,"E43");var subQ10=sQuery(id+"F0.wireOp",EDGE,"E40");var subQ11=sQuery(id+"F0.wireOp",EDGE,"E9");var subQ12=sQuery(id+"F0.wireOp",EDGE,"E0.bottom");Q1=makeQuery(id+"F9.boolean.opBoolean","MERGE",EDGE,{"derivedFrom":[makeQuery(id+"F3.boolean.opBoolean","SPLIT",EDGE,{"disambiguationData":[TD([makeQuery(id+"F3.opExtrude","SWEPT_FACE",FACE,{"disambiguationData":[OSD([sQuery(id+"F2.wireOp",EDGE,"E172")])]})])],"derivedFrom":makeQuery(id+"F1.opExtrude","CAP_EDGE",EDGE,{"disambiguationData":[OSD([subQ12,subQ11,subQ10,subQ9,subQ8,subQ7,subQ6,subQ5,subQ4,subQ3,subQ2,subQ1,subQ0])],"isStart":false})}),makeQuery(id+"F9.opExtrude","CAP_EDGE",EDGE,{"disambiguationData":[OSD([sQuery(id+"F8.wireOp",EDGE,"E192")])],"isStart":true})]});}
            var Q2;
            {var subQ0=sQuery(id+"F0.wireOp",EDGE,"E70");var subQ1=sQuery(id+"F0.wireOp",EDGE,"E67");var subQ2=sQuery(id+"F0.wireOp",EDGE,"E64");var subQ3=sQuery(id+"F0.wireOp",EDGE,"E61");var subQ4=sQuery(id+"F0.wireOp",EDGE,"E58");var subQ5=sQuery(id+"F0.wireOp",EDGE,"E55");var subQ6=sQuery(id+"F0.wireOp",EDGE,"E52");var subQ7=sQuery(id+"F0.wireOp",EDGE,"E49");var subQ8=sQuery(id+"F0.wireOp",EDGE,"E46");var subQ9=sQuery(id+"F0.wireOp",EDGE,"E43");var subQ10=sQuery(id+"F0.wireOp",EDGE,"E40");var subQ11=sQuery(id+"F0.wireOp",EDGE,"E9");var subQ12=sQuery(id+"F0.wireOp",EDGE,"E0.bottom");Q2=makeQuery(id+"F9.boolean.opBoolean","MERGE",EDGE,{"derivedFrom":[makeQuery(id+"F3.boolean.opBoolean","SPLIT",EDGE,{"disambiguationData":[TD([makeQuery(id+"F3.opExtrude","SWEPT_FACE",FACE,{"disambiguationData":[OSD([sQuery(id+"F2.wireOp",EDGE,"E170")])]})])],"derivedFrom":makeQuery(id+"F1.opExtrude","CAP_EDGE",EDGE,{"disambiguationData":[OSD([subQ12,subQ11,subQ10,subQ9,subQ8,subQ7,subQ6,subQ5,subQ4,subQ3,subQ2,subQ1,subQ0])],"isStart":false})}),makeQuery(id+"F9.opExtrude","CAP_EDGE",EDGE,{"disambiguationData":[OSD([sQuery(id+"F8.wireOp",EDGE,"E195")])],"isStart":true})]});}
            fillet(context, id + "F10", {"entities" : qUnion([Q0, Q1, Q2]), "radius" : 5.08 * mm, "tangentPropagation" : true, "allowEdgeOverflow" : false});
        }
    });
